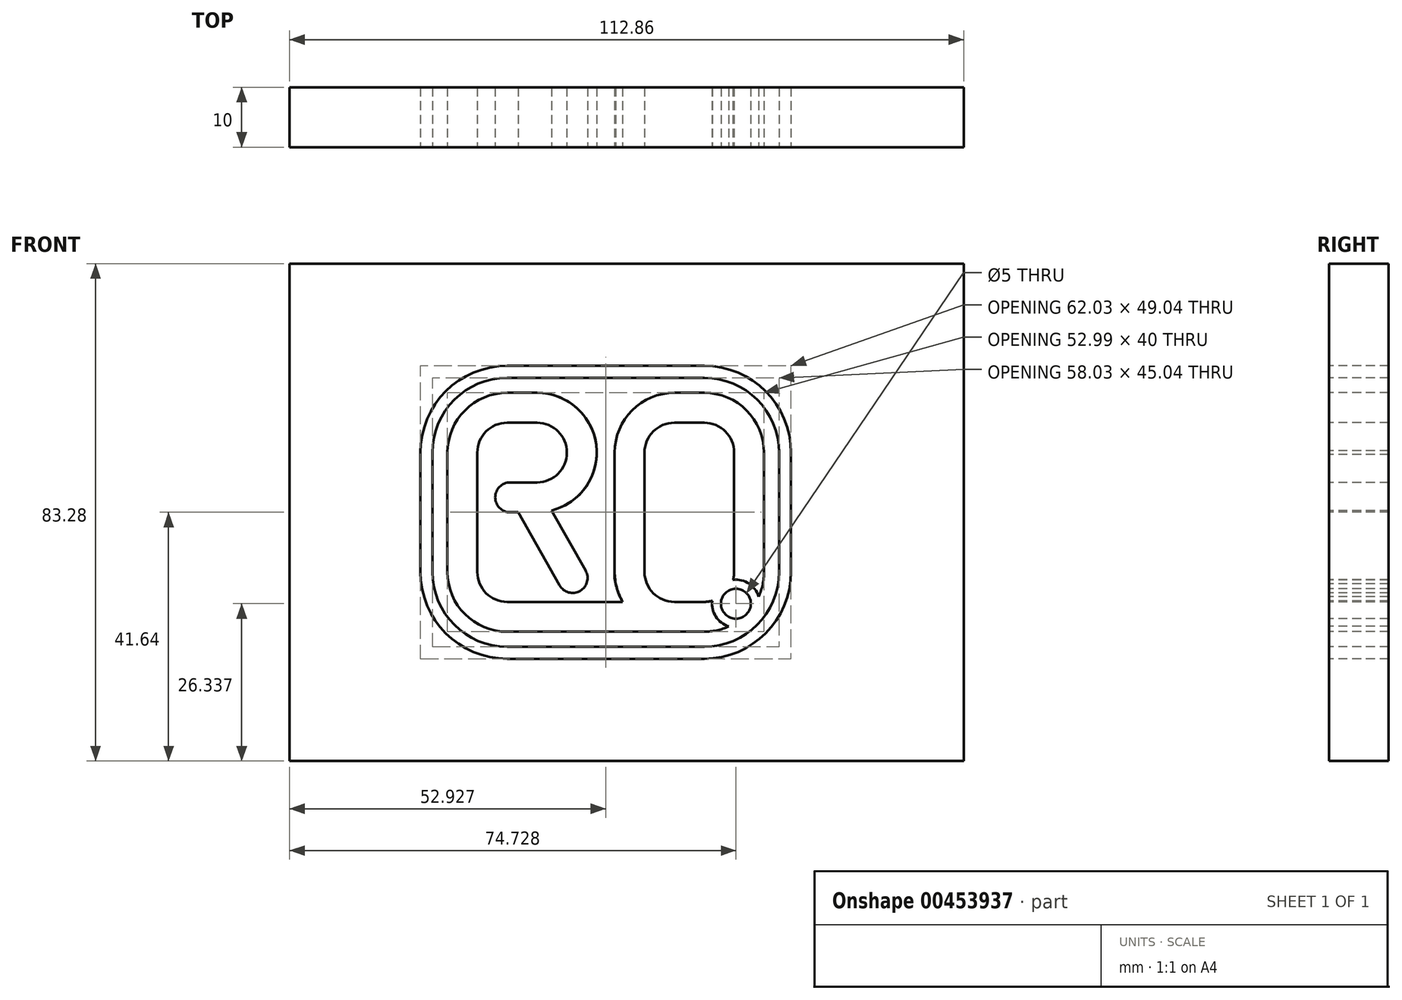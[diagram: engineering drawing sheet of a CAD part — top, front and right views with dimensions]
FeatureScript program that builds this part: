
annotation { "Feature Type Name" : "Feature", "Feature Type Description" : "" }
export const myFeature = defineFeature(function(context is Context, id is Id, definition is map)
    precondition{}
    {
        {
            var Q0;
            Q0=qCreatedBy(makeId("Front.planeOp"),FACE);
            var sketch = newSketch(context, id + "F0", { "sketchPlane" : qUnion([Q0])});
            skPoint(sketch, "E0.middle", {"position": v(0, 0) * mm});
            skLineSegment(sketch, "E1", {"start": v(-25, 10) * mm, "end": v(-25, -10) * mm});
            skLineSegment(sketch, "E2", {"start": v(-2, -20) * mm, "end": v(-0.38, -20) * mm});
            skLineSegment(sketch, "E3", {"start": v(-2, -11) * mm, "end": v(-2, 10) * mm});
            skLineSegment(sketch, "E4", {"start": v(8, 20) * mm, "end": v(13, 20) * mm});
            skLineSegment(sketch, "E5", {"start": v(23, 10) * mm, "end": v(23, -10) * mm});
            skLineSegment(sketch, "E6", {"start": v(13, -20) * mm, "end": v(9, -20) * mm});
            skLineSegment(sketch, "E7", {"start": v(-25, 20) * mm, "end": v(-15, 20) * mm});
            skLineSegment(sketch, "E8", {"start": v(-19.5, 0) * mm, "end": v(-15, 0) * mm});
            skLineSegment(sketch, "E9", {"start": v(-5, 10.33) * mm, "end": v(-5, 10.33) * mm});
            skPoint(sketch, "E10.visualSharp", {"position": v(-5.33, 20) * mm});
            skArc(sketch, "E10.filletArc", {"start": v(-5, 10.33) * mm, "mid": v(-8.05, 17.19) * mm, "end": v(-15, 20) * mm});
            skArc(sketch, "E11.filletArc", {"start": v(-15, 0) * mm, "mid": v(-7.81, 3.05) * mm, "end": v(-5, 10.33) * mm});
            skPoint(sketch, "E12.visualSharp", {"position": v(-3.63, -20) * mm});
            skPoint(sketch, "E13.visualSharp", {"position": v(23, -20) * mm});
            skArc(sketch, "E13.filletArc", {"start": v(13, -20) * mm, "mid": v(15.1, -19.78) * mm, "end": v(17.1, -19.12) * mm});
            skPoint(sketch, "E14.visualSharp", {"position": v(23, 20) * mm});
            skArc(sketch, "E14.filletArc", {"start": v(23, 10) * mm, "mid": v(20.07, 17.07) * mm, "end": v(13, 20) * mm});
            skPoint(sketch, "E15.visualSharp", {"position": v(-2, 20) * mm});
            skArc(sketch, "E15.filletArc", {"start": v(8, 20) * mm, "mid": v(0.92, 17.07) * mm, "end": v(-2, 10) * mm});
            skPoint(sketch, "E16.visualSharp", {"position": v(-2, -20) * mm});
            skArc(sketch, "E17.0", {"start": v(8, 15) * mm, "mid": v(4.46, 13.54) * mm, "end": v(3, 10) * mm});
            skLineSegment(sketch, "E17.1", {"start": v(3, -11) * mm, "end": v(3, 10) * mm});
            skLineSegment(sketch, "E17.2", {"start": v(8, 15) * mm, "end": v(13, 15) * mm});
            skArc(sketch, "E17.4", {"start": v(18, 10) * mm, "mid": v(16.53, 13.54) * mm, "end": v(13, 15) * mm});
            skLineSegment(sketch, "E17.5", {"start": v(18, 10) * mm, "end": v(18, -10) * mm});
            skArc(sketch, "E17.6", {"start": v(13, -15) * mm, "mid": v(13.67, -14.95) * mm, "end": v(14.33, -14.82) * mm});
            skLineSegment(sketch, "E17.7", {"start": v(13, -15) * mm, "end": v(9, -15) * mm});
            skArc(sketch, "E18.1", {"start": v(-15, 5) * mm, "mid": v(-11.44, 6.5) * mm, "end": v(-10, 10.08) * mm});
            skArc(sketch, "E18.2", {"start": v(-10, 10.08) * mm, "mid": v(-11.5, 13.56) * mm, "end": v(-15, 15) * mm});
            skLineSegment(sketch, "E18.3", {"start": v(-20, 15) * mm, "end": v(-15, 15) * mm});
            skLineSegment(sketch, "E19.0", {"start": v(-30, 17.5) * mm, "end": v(-30, -10) * mm});
            skLineSegment(sketch, "E20.0", {"start": v(-1, -15) * mm, "end": v(-0.38, -15) * mm});
            skLineSegment(sketch, "E21", {"start": v(-20, -20) * mm, "end": v(-2, -20) * mm});
            skLineSegment(sketch, "E22", {"start": v(-1, -15) * mm, "end": v(0, -15) * mm});
            skLineSegment(sketch, "E23.0", {"start": v(-20, -15) * mm, "end": v(0, -15) * mm});
            skLineSegment(sketch, "E24", {"start": v(-5, 10.33) * mm, "end": v(-5, 0) * mm});
            skLineSegment(sketch, "E25", {"start": v(0.5, -13.5) * mm, "end": v(0.5, -13.5) * mm});
            skPoint(sketch, "E26.visualSharp", {"position": v(3, -13.5) * mm});
            skArc(sketch, "E26.filletArc", {"start": v(0.5, -13.5) * mm, "mid": v(2.26, -12.77) * mm, "end": v(3, -11) * mm, "construction": true});
            skPoint(sketch, "E27.newPointB", {"position": v(-23.5, -13.5) * mm});
            skArc(sketch, "E27.filletArc", {"start": v(-2, -11) * mm, "mid": v(-1.27, -12.77) * mm, "end": v(0.5, -13.5) * mm});
            skPoint(sketch, "E28.visualSharp", {"position": v(-30, -20) * mm});
            skArc(sketch, "E28.filletArc", {"start": v(-30, -19.5) * mm, "mid": v(-29.85, -19.85) * mm, "end": v(-29.5, -20) * mm});
            skLineSegment(sketch, "E29", {"start": v(-7.28, -12.77) * mm, "end": v(-7.28, -12.77) * mm});
            skArc(sketch, "E30.filletArc", {"start": v(-7.28, -12.77) * mm, "mid": v(-6.55, -11) * mm, "end": v(-7.27, -9.24) * mm});
            skArc(sketch, "E31.filletArc", {"start": v(-11.23, -12.21) * mm, "mid": v(-9.4, -13.48) * mm, "end": v(-7.28, -12.77) * mm});
            skLineSegment(sketch, "E32.0", {"start": v(14.76, -15.3) * mm, "end": v(14.29, -14.83) * mm});
            skPoint(sketch, "E33.newPointB", {"position": v(-25, 20) * mm});
            skPoint(sketch, "E34.visualSharp", {"position": v(-23.5, 5) * mm});
            skPoint(sketch, "E35.visualSharp", {"position": v(-23.5, 0) * mm});
            skLineSegment(sketch, "E36", {"start": v(-30, 10) * mm, "end": v(-30, 17.5) * mm});
            skLineSegment(sketch, "E37", {"start": v(-20, 20) * mm, "end": v(-25, 20) * mm});
            skPoint(sketch, "E38.visualSharp", {"position": v(-30, 20) * mm});
            skArc(sketch, "E38.filletArc", {"start": v(-20, 20) * mm, "mid": v(-27.07, 17.07) * mm, "end": v(-30, 10) * mm});
            skPoint(sketch, "E39", {"position": v(20.07, -17.07) * mm});
            skPoint(sketch, "E40.orphan", {"position": v(16.53, -13.54) * mm});
            skLineSegment(sketch, "E41.trimOffspring", {"start": v(13, -20) * mm, "end": v(-0.38, -20) * mm});
            skPoint(sketch, "E42.newPointB", {"position": v(-25, -20) * mm});
            skArc(sketch, "E42.filletArc", {"start": v(-25, -10) * mm, "mid": v(-23.54, -13.54) * mm, "end": v(-20, -15) * mm});
            skLineSegment(sketch, "E43", {"start": v(-15, 20) * mm, "end": v(8, 20) * mm});
            skLineSegment(sketch, "E44", {"start": v(21.86, -24.52) * mm, "end": v(-20, -24.52) * mm});
            skLineSegment(sketch, "E45", {"start": v(27.51, -22.02) * mm, "end": v(27.51, -18.86) * mm});
            skLineSegment(sketch, "E46", {"start": v(13, 24.52) * mm, "end": v(-20, 24.52) * mm});
            skLineSegment(sketch, "E47", {"start": v(-34.52, -10) * mm, "end": v(-34.52, 10) * mm});
            skPoint(sketch, "E48.orphan", {"position": v(17.43, -17.97) * mm});
            skPoint(sketch, "E49.orphan", {"position": v(13.35, -13.89) * mm});
            skArc(sketch, "E50.0", {"start": v(27.51, 10) * mm, "mid": v(23.26, 20.27) * mm, "end": v(13, 24.52) * mm});
            skArc(sketch, "E51.0", {"start": v(25.51, 10) * mm, "mid": v(21.85, 18.85) * mm, "end": v(13, 22.52) * mm});
            skLineSegment(sketch, "E52.0", {"start": v(25.51, -22.07) * mm, "end": v(25.51, -18.99) * mm});
            skLineSegment(sketch, "E53.0", {"start": v(25.02, -22.52) * mm, "end": v(21.98, -22.52) * mm});
            skLineSegment(sketch, "E54.0", {"start": v(-32.52, -10) * mm, "end": v(-32.52, 10) * mm});
            skLineSegment(sketch, "E55.0", {"start": v(13, 22.52) * mm, "end": v(-20, 22.52) * mm});
            skPoint(sketch, "E56.visualSharp", {"position": v(-32.52, 22.52) * mm});
            skArc(sketch, "E56.filletArc", {"start": v(-20, 22.52) * mm, "mid": v(-28.85, 18.85) * mm, "end": v(-32.52, 10) * mm});
            skArc(sketch, "E57.0", {"start": v(-20, 24.52) * mm, "mid": v(-30.27, 20.27) * mm, "end": v(-34.52, 10) * mm});
            skPoint(sketch, "E58.visualSharp", {"position": v(-32.52, -22.52) * mm});
            skLineSegment(sketch, "E59", {"start": v(26.51, -15) * mm, "end": v(26.51, -16.32) * mm});
            skLineSegment(sketch, "E60.0", {"start": v(18.1, -20.77) * mm, "end": v(22.19, -24.85) * mm, "construction": true});
            skLineSegment(sketch, "E61.0", {"start": v(23.76, -15.1) * mm, "end": v(27.84, -19.2) * mm, "construction": true});
            skLineSegment(sketch, "E62.trimOffspring", {"start": v(25.51, -14) * mm, "end": v(25.51, 10) * mm});
            skLineSegment(sketch, "E63.trimOffspring", {"start": v(27.51, -14) * mm, "end": v(27.51, 33) * mm});
            skLineSegment(sketch, "E64.trimOffspring", {"start": v(19.86, -22.52) * mm, "end": v(-20, -22.52) * mm});
            skLineSegment(sketch, "E65", {"start": v(21.86, -24.52) * mm, "end": v(25.02, -24.52) * mm});
            skLineSegment(sketch, "E66", {"start": v(27.51, -14) * mm, "end": v(27.51, -22.02) * mm});
            skLineSegment(sketch, "E67.bottom", {"start": v(-56.43, 41.64) * mm, "end": v(56.43, 41.64) * mm});
            skLineSegment(sketch, "E67.top", {"start": v(-56.43, -41.64) * mm, "end": v(56.43, -41.64) * mm});
            skLineSegment(sketch, "E67.left", {"start": v(-56.43, 41.64) * mm, "end": v(-56.43, -41.64) * mm});
            skLineSegment(sketch, "E67.right", {"start": v(56.43, 41.64) * mm, "end": v(56.43, -41.64) * mm});
            skLineSegment(sketch, "E68", {"start": v(0, 0) * mm, "end": v(0, -38.7) * mm, "construction": true});
            skLineSegment(sketch, "E69", {"start": v(0, 0) * mm, "end": v(33.56, 0) * mm, "construction": true});
            skArc(sketch, "E70.filletArc", {"start": v(-20, 15) * mm, "mid": v(-23.54, 13.54) * mm, "end": v(-25, 10) * mm});
            skArc(sketch, "E71.0", {"start": v(-30, -10) * mm, "mid": v(-27.07, -17.07) * mm, "end": v(-20, -20) * mm});
            skArc(sketch, "E72.0", {"start": v(-34.52, -10) * mm, "mid": v(-30.27, -20.27) * mm, "end": v(-20, -24.52) * mm});
            skArc(sketch, "E73.0", {"start": v(-32.52, -10) * mm, "mid": v(-28.85, -18.85) * mm, "end": v(-20, -22.52) * mm});
            skLineSegment(sketch, "E74", {"start": v(-15, 5) * mm, "end": v(-19.5, 5) * mm});
            skLineSegment(sketch, "E75", {"start": v(-23.5, 2.5) * mm, "end": v(-23.5, 2.5) * mm});
            skArc(sketch, "E76.filletArc", {"start": v(-21, 5) * mm, "mid": v(-22.77, 4.27) * mm, "end": v(-23.5, 2.5) * mm, "construction": true});
            skArc(sketch, "E77.filletArc", {"start": v(-23.5, 2.5) * mm, "mid": v(-22.77, 0.73) * mm, "end": v(-21, 0) * mm, "construction": true});
            skPoint(sketch, "E78.startSnap0", {"position": v(-6.55, -11) * mm});
            skLineSegment(sketch, "E79", {"start": v(-22.87, 0.84) * mm, "end": v(-10.92, -12.66) * mm, "construction": true});
            skLineSegment(sketch, "E80.0", {"start": v(-19.13, 4.16) * mm, "end": v(-7.17, -9.34) * mm, "construction": true});
            skArc(sketch, "E81.0", {"start": v(13, -22.52) * mm, "mid": v(21.85, -18.85) * mm, "end": v(25.51, -10) * mm});
            skArc(sketch, "E82.0", {"start": v(13, -24.52) * mm, "mid": v(23.26, -20.27) * mm, "end": v(27.51, -10) * mm});
            skCircle(sketch, "E83", {"center": v(18.3, -15.3) * mm, "radius": 2.5 * mm});
            skLineSegment(sketch, "E84", {"start": v(-21, 5) * mm, "end": v(-21, 0) * mm, "construction": true});
            skLineSegment(sketch, "E85", {"start": v(-21, 5) * mm, "end": v(-11.1, -12.46) * mm});
            skLineSegment(sketch, "E86.0", {"start": v(-16.65, 7.47) * mm, "end": v(-6.74, -10) * mm});
            skLineSegment(sketch, "E87", {"start": v(-22, 7.3) * mm, "end": v(-22, -4.59) * mm});
            skLineSegment(sketch, "E88", {"start": v(-28.56, 2.5) * mm, "end": v(-6.16, 2.5) * mm, "construction": true});
            skCircle(sketch, "E89", {"center": v(-19.5, 2.5) * mm, "radius": 2.5 * mm});
            skLineSegment(sketch, "E90", {"start": v(16.53, -13.54) * mm, "end": v(20.07, -17.07) * mm});
            skArc(sketch, "E91.0", {"start": v(14.33, -14.82) * mm, "mid": v(14.94, -17.47) * mm, "end": v(17.1, -19.12) * mm});
            skLineSegment(sketch, "E92", {"start": v(10.5, 15) * mm, "end": v(10.5, 5.39) * mm, "construction": true});
            skArc(sketch, "E93.MirrorCS", {"start": v(8, -15) * mm, "mid": v(4.46, -13.54) * mm, "end": v(3, -10) * mm});
            skArc(sketch, "E94.MirrorCS", {"start": v(8, -20) * mm, "mid": v(0.92, -17.07) * mm, "end": v(-2, -10) * mm});
            skArc(sketch, "E95.trimOffspring", {"start": v(22.11, -14.1) * mm, "mid": v(20.46, -11.94) * mm, "end": v(17.81, -11.33) * mm});
            skArc(sketch, "E96.trimOffspring", {"start": v(22.11, -14.1) * mm, "mid": v(22.77, -12.1) * mm, "end": v(23, -10) * mm});
            skArc(sketch, "E97.trimOffspring", {"start": v(17.81, -11.33) * mm, "mid": v(17.95, -10.67) * mm, "end": v(18, -10) * mm});
            skLineSegment(sketch, "E98.trimOffspring", {"start": v(8, -15) * mm, "end": v(9, -15) * mm});
            skSolve(sketch);
        }
        {
            var Q0;
            Q0=makeQuery(id+"F0.imprint","IMPRINT",FACE,{"disambiguationData":[TD([[makeQuery(id+"F0.imprint","IMPRINT",EDGE,{"derivedFrom":sQuery(id+"F0.wireOp",EDGE,"E1")}),-1.0]])]});
            var Q1;
            {var subQ6=sQuery(id+"F0.wireOp",EDGE,"8dgEX87s-OnN3-UPAw-RyUf-tcfM0RuKeMZf");Q1=makeQuery(id+"F0.imprint","IMPRINT",FACE,{"disambiguationData":[TD([[makeQuery(id+"F0.imprint","IMPRINT",EDGE,{"derivedFrom":subQ6}),1.0]])]});}
            var Q2;
            {var subQ0=sQuery(id+"F0.wireOp",EDGE,"S70SFG3v-wlmV-iE8w-7gkR-MiBzXbBwRlH9");var subQ1=makeQuery(id+"F0.imprint","INTERSECT",VERTEX,{"derivedFrom":[sQuery(id+"F0.wireOp",EDGE,"c0c087a9-fd36-4214-a694-875f0f01d769.0"),subQ0]});Q2=makeQuery(id+"F0.imprint","IMPRINT",FACE,{"disambiguationData":[TD([[makeQuery(id+"F0.imprint","IMPRINT",EDGE,{"disambiguationData":[TD([[subQ1,-1.0]])],"derivedFrom":subQ0}),1.0]])]});}
            var Q3;
            {var subQ1=sQuery(id+"F0.wireOp",EDGE,"c0c087a9-fd36-4214-a694-875f0f01d769.0");Q3=makeQuery(id+"F0.imprint","IMPRINT",FACE,{"disambiguationData":[TD([[makeQuery(id+"F0.imprint","IMPRINT",EDGE,{"derivedFrom":subQ1}),-1.0]])]});}
            var Q4;
            {var subQ0=sQuery(id+"F0.wireOp",EDGE,"E0.bottom");Q4=makeQuery(id+"F0.imprint","IMPRINT",FACE,{"disambiguationData":[TD([[makeQuery(id+"F0.imprint","IMPRINT",EDGE,{"derivedFrom":subQ0}),-1.0]])]});}
            var Q5;
            {var subQ0=sQuery(id+"F0.wireOp",EDGE,"E0.bottom");Q5=makeQuery(id+"F0.imprint","IMPRINT",FACE,{"disambiguationData":[TD([[makeQuery(id+"F0.imprint","IMPRINT",EDGE,{"derivedFrom":subQ0}),1.0]])]});}
            var Q6;
            {var subQ3=sQuery(id+"F0.wireOp",EDGE,"E8");var subQ7=sQuery(id+"F0.wireOp",EDGE,"E11.filletArc");var subQ8=makeQuery(id+"F0.imprint","INTERSECT",VERTEX,{"derivedFrom":[subQ3,subQ7]});Q6=makeQuery(id+"F0.imprint","IMPRINT",FACE,{"disambiguationData":[TD([[makeQuery(id+"F0.imprint","IMPRINT",EDGE,{"disambiguationData":[TD([[subQ8,1.0]])],"derivedFrom":subQ3}),1.0]])]});}
            var Q7;
            {var subQ4=sQuery(id+"F0.wireOp",EDGE,"E76.filletArc");Q7=makeQuery(id+"F0.imprint","IMPRINT",FACE,{"disambiguationData":[TD([[makeQuery(id+"F0.imprint","IMPRINT",EDGE,{"derivedFrom":subQ4}),1.0]])]});}
            var Q8;
            {var subQ0=sQuery(id+"F0.wireOp",EDGE,"E31.filletArc");Q8=makeQuery(id+"F0.imprint","IMPRINT",FACE,{"disambiguationData":[TD([[makeQuery(id+"F0.imprint","IMPRINT",EDGE,{"derivedFrom":subQ0}),1.0]])]});}
            var Q9;
            Q9=makeQuery(id+"F0.imprint","IMPRINT",FACE,{"disambiguationData":[TD([[makeQuery(id+"F0.imprint","IMPRINT",EDGE,{"derivedFrom":sQuery(id+"F0.wireOp",EDGE,"E83")}),1.0]])]});
            var Q10;
            {var subQ0=sQuery(id+"F0.wireOp",EDGE,"E88");var subQ1=sQuery(id+"F0.wireOp",EDGE,"E11.filletArc");var subQ2=makeQuery(id+"F0.imprint","INTERSECT",VERTEX,{"derivedFrom":[subQ1,subQ0]});Q10=makeQuery(id+"F0.imprint","IMPRINT",FACE,{"disambiguationData":[TD([[makeQuery(id+"F0.imprint","IMPRINT",EDGE,{"disambiguationData":[TD([[subQ2,1.0]])],"derivedFrom":subQ1}),1.0]])]});}
            var Q11;
            {var subQ0=sQuery(id+"F0.wireOp",EDGE,"E89");var subQ1=sQuery(id+"F0.wireOp",EDGE,"E74");var subQ2=makeQuery(id+"F0.imprint","INTERSECT",VERTEX,{"derivedFrom":[subQ1,subQ0]});Q11=makeQuery(id+"F0.imprint","IMPRINT",FACE,{"disambiguationData":[TD([[makeQuery(id+"F0.imprint","IMPRINT",EDGE,{"disambiguationData":[TD([[subQ2,1.0]])],"derivedFrom":subQ1}),1.0]])]});}
            var Q12;
            {var subQ0=sQuery(id+"F0.wireOp",EDGE,"E88");var subQ1=sQuery(id+"F0.wireOp",EDGE,"E85");var subQ2=makeQuery(id+"F0.imprint","INTERSECT",VERTEX,{"derivedFrom":[subQ1,subQ0]});Q12=makeQuery(id+"F0.imprint","IMPRINT",FACE,{"disambiguationData":[TD([[makeQuery(id+"F0.imprint","IMPRINT",EDGE,{"disambiguationData":[TD([[subQ2,-1.0]])],"derivedFrom":subQ1}),-1.0]])]});}
            var Q13;
            {var subQ0=sQuery(id+"F0.wireOp",EDGE,"E89");var subQ1=sQuery(id+"F0.wireOp",EDGE,"E85");var subQ2=makeQuery(id+"F0.imprint","INTERSECT",VERTEX,{"disambiguationData":[OD(0.0)],"derivedFrom":[subQ1,subQ0]});Q13=makeQuery(id+"F0.imprint","IMPRINT",FACE,{"disambiguationData":[TD([[makeQuery(id+"F0.imprint","IMPRINT",EDGE,{"disambiguationData":[TD([[subQ2,-1.0]])],"derivedFrom":subQ1}),-1.0]])]});}
            var Q14;
            {var subQ0=sQuery(id+"F0.wireOp",EDGE,"E89");var subQ1=sQuery(id+"F0.wireOp",EDGE,"E85");var subQ2=makeQuery(id+"F0.imprint","INTERSECT",VERTEX,{"disambiguationData":[OD(0.0)],"derivedFrom":[subQ1,subQ0]});Q14=makeQuery(id+"F0.imprint","IMPRINT",FACE,{"disambiguationData":[TD([[makeQuery(id+"F0.imprint","IMPRINT",EDGE,{"disambiguationData":[TD([[subQ2,-1.0]])],"derivedFrom":subQ1}),1.0]])]});}
            var Q15;
            {var subQ0=sQuery(id+"F0.wireOp",EDGE,"E88");var subQ1=sQuery(id+"F0.wireOp",EDGE,"E85");var subQ2=makeQuery(id+"F0.imprint","INTERSECT",VERTEX,{"derivedFrom":[subQ1,subQ0]});Q15=makeQuery(id+"F0.imprint","IMPRINT",FACE,{"disambiguationData":[TD([[makeQuery(id+"F0.imprint","IMPRINT",EDGE,{"disambiguationData":[TD([[subQ2,-1.0]])],"derivedFrom":subQ1}),1.0]])]});}
            var Q16;
            {var subQ0=sQuery(id+"F0.wireOp",EDGE,"E89");var subQ1=sQuery(id+"F0.wireOp",EDGE,"E8");var subQ2=makeQuery(id+"F0.imprint","INTERSECT",VERTEX,{"derivedFrom":[subQ1,subQ0]});Q16=makeQuery(id+"F0.imprint","IMPRINT",FACE,{"disambiguationData":[TD([[makeQuery(id+"F0.imprint","IMPRINT",EDGE,{"disambiguationData":[TD([[subQ2,-1.0]])],"derivedFrom":subQ1}),1.0]])]});}
            var Q17;
            Q17=makeQuery(id+"F0.imprint","IMPRINT",FACE,{"disambiguationData":[TD([[makeQuery(id+"F0.imprint","IMPRINT",EDGE,{"derivedFrom":sQuery(id+"F0.wireOp",EDGE,"E4")}),-1.0]])]});
            extrude(context, id + "F1", {"entities" : qUnion([Q0, Q1, Q2, Q3, Q4, Q5, Q6, Q7, Q8, Q9, Q10, Q11, Q12, Q13, Q14, Q15, Q16, Q17]), "oppositeDirection" : true, "depth" : 10 * mm});
        }
        {
            var Q0;
            Q0=makeQuery(id+"F0.imprint","IMPRINT",FACE,{"disambiguationData":[TD([[makeQuery(id+"F0.imprint","IMPRINT",EDGE,{"derivedFrom":sQuery(id+"F0.wireOp",EDGE,"E1")}),1.0]])]});
            var Q1;
            {var subQ16=sQuery(id+"F0.wireOp",EDGE,"E2");Q1=makeQuery(id+"F0.imprint","IMPRINT",FACE,{"disambiguationData":[TD([[makeQuery(id+"F0.imprint","IMPRINT",EDGE,{"derivedFrom":subQ16}),-1.0]])]});}
            extrude(context, id + "F2", {"entities" : qUnion([Q0, Q1]), "oppositeDirection" : true, "depth" : 10 * mm});
        }
        {
            var Q0;
            Q0=makeQuery(id+"F0.imprint","IMPRINT",FACE,{"disambiguationData":[TD([[makeQuery(id+"F0.imprint","IMPRINT",EDGE,{"derivedFrom":sQuery(id+"F0.wireOp",EDGE,"E46")}),1.0]])]});
            var Q1;
            {var subQ0=sQuery(id+"F0.wireOp",EDGE,"aTrX08yB-o83u-csdW-HvKf-6qn933KxLSEO");var subQ2=makeQuery(id+"F0.imprint","IMPRINT",VERTEX,{"derivedFrom":subQ0});Q1=makeQuery(id+"F0.imprint","IMPRINT",FACE,{"disambiguationData":[TD([[makeQuery(id+"F0.imprint","IMPRINT",EDGE,{"disambiguationData":[TD([[subQ2,-1.0]])],"derivedFrom":subQ0}),1.0]])]});}
            var Q2;
            {var subQ0=sQuery(id+"F0.wireOp",EDGE,"orb3SBHr-i0Mj-h6B2-otKM-5Ab6eh35dINg");var subQ3=makeQuery(id+"F0.imprint","IMPRINT",VERTEX,{"derivedFrom":subQ0});Q2=makeQuery(id+"F0.imprint","IMPRINT",FACE,{"disambiguationData":[TD([[makeQuery(id+"F0.imprint","IMPRINT",EDGE,{"disambiguationData":[TD([[subQ3,1.0]])],"derivedFrom":subQ0}),1.0]])]});}
            extrude(context, id + "F3", {"entities" : qUnion([Q0, Q1, Q2]), "oppositeDirection" : true, "depth" : 10 * mm});
        }
        {
            var Q0;
            Q0=makeQuery(id+"F0.imprint","IMPRINT",FACE,{"disambiguationData":[TD([[makeQuery(id+"F0.imprint","IMPRINT",EDGE,{"derivedFrom":sQuery(id+"F0.wireOp",EDGE,"E46")}),-1.0]])]});
            extrude(context, id + "F4", {"entities" : qUnion([Q0]), "oppositeDirection" : true, "depth" : 10 * mm});
        }
    });
